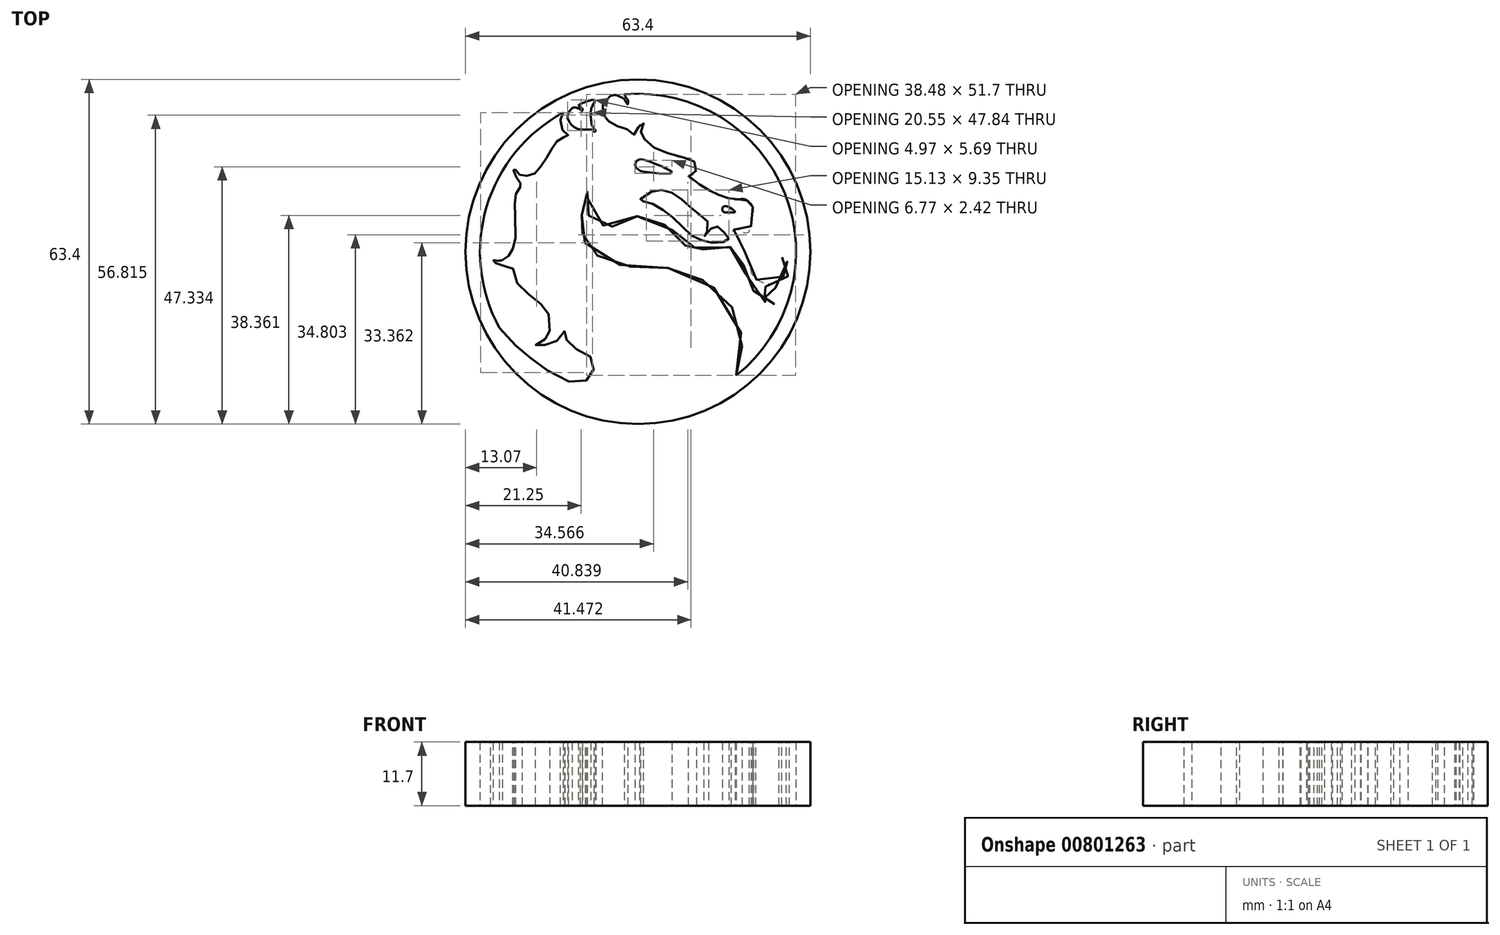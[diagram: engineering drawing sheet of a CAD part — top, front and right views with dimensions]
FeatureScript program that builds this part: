
annotation { "Feature Type Name" : "Feature", "Feature Type Description" : "" }
export const myFeature = defineFeature(function(context is Context, id is Id, definition is map)
    precondition{}
    {
        {
            var Q0;
            Q0=qCreatedBy(makeId("Top.planeOp"),FACE);
            var sketch = newSketch(context, id + "F0", { "sketchPlane" : qUnion([Q0])});
            skCircle(sketch, "E0", {"center": v(0, 0) * mm, "radius": 31.7 * mm});
            skArc(sketch, "E1", {"start": v(-7.96, 27.95) * mm, "mid": v(-9.46, 27.48) * mm, "end": v(-10.93, 26.93) * mm});
            skFitSpline(sketch, "E2", {"points": [v(-25.5, -13.95) * mm, v(-22.7, -17.05) * mm, v(-20.86, -18.67) * mm, v(-18.36, -20.6) * mm, v(-15.95, -22.27) * mm, v(-12.36, -23.98) * mm, v(-10.16, -23.98) * mm, v(-8.94, -23.23) * mm, v(-8.32, -22.18) * mm, v(-8.02, -20.95) * mm, v(-8.32, -19.72) * mm, v(-9.99, -18.54) * mm, v(-11.26, -17.93) * mm, v(-12.22, -17.23) * mm, v(-13.1, -16.26) * mm, v(-13.4, -15.12) * mm, v(-13.4, -14.46) * mm, v(-13.67, -14.9) * mm, v(-14.24, -15.78) * mm, v(-15.03, -16.48) * mm, v(-15.9, -16.96) * mm, v(-17.22, -17.18) * mm, v(-18.06, -17.31) * mm, v(-18.85, -17.31) * mm, v(-18.67, -17.05) * mm, v(-17.88, -16.61) * mm, v(-17.14, -16.13) * mm, v(-16.74, -15.7) * mm, v(-16.52, -15.16) * mm, v(-16.26, -14.6) * mm, v(-16.21, -12.23) * mm, v(-16.54, -11.21) * mm, v(-17.22, -10.16) * mm, v(-18.21, -9.34) * mm, v(-19.41, -8.4) * mm, v(-20.9, -7.06) * mm, v(-22.02, -5.97) * mm, v(-22.84, -4.63) * mm, v(-22.95, -3.05) * mm, v(-22.8, -2.6) * mm, v(-23.37, -2.72) * mm, v(-24.22, -2.82) * mm, v(-25.2, -2.63) * mm, v(-26.25, -2.07) * mm, v(-27.1, -1.5) * mm, v(-27.02, -1.3) * mm, v(-26.62, -1.56) * mm], "startDerivative": vector(73.14, -85.9) * mm, "endDerivative": vector(33.12, -30.6) * mm});
            skArc(sketch, "E3", {"start": v(-26.62, -1.56) * mm, "mid": v(-25.76, -1.65) * mm, "end": v(-24.9, -1.56) * mm});
            skFitSpline(sketch, "E4", {"points": [v(-24.9, -1.56) * mm, v(-24.22, -1.18) * mm, v(-23.58, -0.47) * mm, v(-23.09, 0.44) * mm, v(-22.64, 1.15) * mm, v(-22.61, 7.55) * mm, v(-22.64, 8.78) * mm, v(-22.5, 10.34) * mm, v(-22.04, 11.46) * mm, v(-21.33, 12.17) * mm, v(-21.23, 12.27) * mm, v(-21.7, 12.74) * mm, v(-22.17, 13.42) * mm, v(-22.64, 14.17) * mm, v(-22.87, 14.98) * mm, v(-22.87, 15.55) * mm, v(-22.59, 15.16) * mm, v(-22.12, 14.54) * mm, v(-21.67, 14.15) * mm, v(-20.92, 13.94) * mm, v(-19.85, 14.02) * mm, v(-18.9, 14.46) * mm, v(-18.1, 15.37) * mm, v(-17.27, 16.54) * mm, v(-16.2, 18.27) * mm, v(-15.6, 19.39) * mm, v(-14.82, 20.4) * mm, v(-13.93, 21.03) * mm, v(-12.94, 21.13) * mm, v(-12.76, 21.34) * mm, v(-13.23, 21.6) * mm, v(-13.9, 22.49) * mm, v(-14.24, 24.05) * mm, v(-14, 25.12) * mm, v(-13.7, 25.63) * mm, v(-13.68, 25.64) * mm, v(-13.7, 25.63) * mm], "startDerivative": vector(27.03, 13) * mm, "endDerivative": vector(-4.63, -2.23) * mm});
            skFitSpline(sketch, "E5", {"points": [v(-7.96, 27.95) * mm, v(-7.98, 27.45) * mm, v(-8.51, 26.58) * mm, v(-8.66, 25.66) * mm, v(-8.64, 24.6) * mm, v(-8.59, 23.87) * mm, v(-8.35, 23.06) * mm, v(-8.01, 22.6) * mm, v(-7.74, 22.29) * mm, v(-7.94, 22.07) * mm, v(-8.42, 22.43) * mm, v(-8.9, 22.47) * mm, v(-10.1, 22.45) * mm, v(-11.04, 22.56) * mm, v(-11.98, 23.08) * mm, v(-12.59, 23.82) * mm, v(-12.95, 24.76) * mm, v(-12.72, 25.66) * mm, v(-11.93, 26.5) * mm, v(-11, 26.4) * mm, v(-10.5, 26.12) * mm, v(-10.36, 25.83) * mm, v(-10.19, 26.21) * mm, v(-10.45, 26.55) * mm, v(-10.8, 26.8) * mm, v(-10.93, 26.93) * mm, v(-7.96, 27.95) * mm]});
            skFitSpline(sketch, "E6", {"points": [v(-2.48, 28.95) * mm, v(-2.35, 28.65) * mm, v(-2.13, 28.23) * mm, v(-1.99, 28.1) * mm, v(-1.84, 27.77) * mm, v(-1.9, 27.08) * mm, v(-2.17, 27.53) * mm, v(-2.65, 28.17) * mm, v(-3.07, 28.43) * mm, v(-3.52, 28.61) * mm, v(-3.9, 28.8) * mm, v(-5.2, 28.6) * mm, v(-6, 27.86) * mm, v(-6.43, 27.08) * mm, v(-6.5, 26.48) * mm, v(-6.48, 25.57) * mm, v(-6.28, 25.02) * mm, v(-5.99, 24.56) * mm, v(-5.4, 24.02) * mm, v(-4.7, 23.6) * mm, v(-3.96, 23.23) * mm, v(-3.33, 22.92) * mm, v(-2.48, 22.7) * mm, v(-1.7, 22.35) * mm, v(-1.1, 21.89) * mm, v(-0.75, 21.52) * mm, v(-0.46, 22.2) * mm, v(-0.16, 22.68) * mm, v(0.26, 23.12) * mm, v(0.69, 23.7) * mm, v(1, 23.71) * mm, v(1.02, 23.71) * mm, v(0.96, 23.23) * mm, v(0.72, 22.72) * mm, v(0.56, 21.98) * mm, v(0.72, 21.39) * mm, v(0.94, 21.02) * mm, v(1.38, 20.55) * mm, v(2.37, 19.56) * mm, v(3.61, 18.87) * mm, v(5.26, 18.2) * mm, v(7.33, 17.45) * mm, v(9.38, 17.26) * mm, v(10.03, 16.9) * mm, v(10.74, 15.96) * mm, v(10.78, 15.4) * mm, v(10.53, 14.66) * mm, v(9.97, 14.25) * mm, v(9.57, 14) * mm, v(9.29, 13.82) * mm, v(10.76, 12.74) * mm, v(12.49, 11.67) * mm, v(13.12, 11.27) * mm, v(13.74, 10.96) * mm, v(14.4, 10.7) * mm, v(15.2, 10.29) * mm, v(16.17, 9.97) * mm, v(16.86, 9.8) * mm, v(17.82, 9.66) * mm, v(18.56, 9.64) * mm, v(19.11, 9.7) * mm, v(19.73, 9.59) * mm, v(20.34, 9.22) * mm, v(20.81, 8.74) * mm, v(21.1, 8.24) * mm, v(21.09, 8.23) * mm], "startDerivative": vector(11.35, -25.78) * mm, "endDerivative": vector(-1.39, -4.3) * mm});
            skFitSpline(sketch, "E7", {"points": [v(21.1, 8.23) * mm, v(21.3, 7.6) * mm, v(20.78, 6.66) * mm, v(20.5, 6.47) * mm, v(20.73, 6.03) * mm, v(20.84, 5.17) * mm, v(20.42, 3.7) * mm, v(19.9, 3.18) * mm, v(19.43, 3.6) * mm, v(18.65, 3.98) * mm, v(17.69, 4.04) * mm, v(17.2, 3.96) * mm, v(17.87, 3.36) * mm, v(18.64, 2.35) * mm, v(19.33, 0.75) * mm, v(20, -0.85) * mm, v(20.52, -2.6) * mm, v(21.1, -4.44) * mm, v(22.36, -5.44) * mm, v(23.93, -5.93) * mm, v(25.25, -5.72) * mm, v(26.43, -4.89) * mm, v(27.16, -3.5) * mm, v(27.1, -2.17) * mm, v(26.47, -1.03) * mm, v(27.2, -1.48) * mm, v(27.8, -2.9) * mm, v(27.55, -4.57) * mm, v(26.36, -6.07) * mm, v(24.24, -6.66) * mm, v(21.77, -6.04) * mm, v(22.3, -7.53) * mm, v(24.03, -8.79) * mm, v(25.7, -9.27) * mm, v(25.95, -9.48) * mm, v(24.62, -9.59) * mm, v(22.85, -8.96) * mm, v(21.5, -7.57) * mm, v(20.27, -5.51) * mm, v(19.61, -3.29) * mm, v(18.88, -0.78) * mm, v(17.77, 1.17) * mm, v(16.69, 0.65) * mm, v(14.22, -0.26) * mm, v(11.82, 0.5) * mm, v(10.08, 0.68) * mm, v(9.17, 0.37) * mm, v(8.69, 1.27) * mm, v(6.84, 3.57) * mm, v(4.86, 4.96) * mm, v(2.28, 6.42) * mm, v(0, 6.56) * mm, v(-2.42, 5.7) * mm, v(-4.16, 4.75) * mm, v(-6.28, 4.79) * mm, v(-8.33, 5.8) * mm, v(-9.44, 7.64) * mm, v(-9.44, 10.32) * mm, v(-9.24, 11.02) * mm, v(-9.97, 10.11) * mm, v(-10.56, 8.23) * mm, v(-10.04, 6.21) * mm, v(-9.37, 5.38) * mm, v(-9.86, 4.82) * mm, v(-10.07, 2.63) * mm, v(-9.1, 0.71) * mm, v(-7.29, -0.82) * mm, v(-3.42, -2.35) * mm, v(-0.43, -2.8) * mm, v(4.1, -2.8) * mm, v(8.3, -3.67) * mm, v(12.06, -5.3) * mm, v(15.89, -8.5) * mm, v(18.4, -12.47) * mm, v(19.16, -17.42) * mm, v(18.9, -20.57) * mm, v(18.08, -22.75) * mm, v(18.05, -22.78) * mm], "startDerivative": vector(44.78, -70.7) * mm, "endDerivative": vector(-14.23, -4.64) * mm});
            skPoint(sketch, "E8", {"position": v(-12.1, 26.41) * mm});
            skPoint(sketch, "E9", {"position": v(-11.83, 26.52) * mm});
            skPoint(sketch, "E10", {"position": v(-13.74, 25.58) * mm});
            skFitSpline(sketch, "E11.trimOffspring", {"points": [v(-2.48, 28.95) * mm, v(-2.35, 28.65) * mm, v(-2.13, 28.23) * mm, v(-1.99, 28.1) * mm, v(-1.84, 27.77) * mm, v(-1.9, 27.08) * mm, v(-2.17, 27.53) * mm, v(-2.65, 28.17) * mm, v(-3.07, 28.43) * mm, v(-3.52, 28.61) * mm, v(-3.9, 28.8) * mm, v(-5.2, 28.6) * mm, v(-6, 27.86) * mm, v(-6.43, 27.08) * mm, v(-6.5, 26.48) * mm, v(-6.48, 25.57) * mm, v(-6.28, 25.02) * mm, v(-5.99, 24.56) * mm, v(-5.4, 24.02) * mm, v(-4.7, 23.6) * mm, v(-3.96, 23.23) * mm, v(-3.33, 22.92) * mm, v(-2.48, 22.7) * mm, v(-1.7, 22.35) * mm, v(-1.1, 21.89) * mm, v(-0.75, 21.52) * mm, v(-0.46, 22.2) * mm, v(-0.16, 22.68) * mm, v(0.26, 23.12) * mm, v(0.69, 23.7) * mm, v(1, 23.71) * mm, v(1.02, 23.71) * mm, v(0.96, 23.23) * mm, v(0.72, 22.72) * mm, v(0.56, 21.98) * mm, v(0.72, 21.39) * mm, v(0.94, 21.02) * mm, v(1.38, 20.55) * mm, v(2.37, 19.56) * mm, v(3.61, 18.87) * mm, v(5.26, 18.2) * mm, v(7.33, 17.45) * mm, v(9.38, 17.26) * mm, v(10.03, 16.9) * mm, v(10.74, 15.96) * mm, v(10.78, 15.4) * mm, v(10.53, 14.66) * mm, v(9.97, 14.25) * mm, v(9.57, 14) * mm, v(9.29, 13.82) * mm, v(10.76, 12.74) * mm, v(12.49, 11.67) * mm, v(13.12, 11.27) * mm, v(13.74, 10.96) * mm, v(14.4, 10.7) * mm, v(15.2, 10.29) * mm, v(16.17, 9.97) * mm, v(16.86, 9.8) * mm, v(17.82, 9.66) * mm, v(18.56, 9.64) * mm, v(19.11, 9.7) * mm, v(19.73, 9.59) * mm, v(20.34, 9.22) * mm, v(20.81, 8.74) * mm, v(21.1, 8.24) * mm, v(21.09, 8.23) * mm], "startDerivative": vector(11.35, -25.78) * mm, "endDerivative": vector(-1.39, -4.3) * mm});
            skArc(sketch, "E12.trimOffspring", {"start": v(-3.9, 28.8) * mm, "mid": v(-4.55, 28.7) * mm, "end": v(-5.2, 28.6) * mm});
            skArc(sketch, "E13.trimOffspring", {"start": v(18.08, -22.75) * mm, "mid": v(27, 10.74) * mm, "end": v(-2.48, 28.95) * mm});
            skLineSegment(sketch, "E14", {"start": v(-12.1, 26.41) * mm, "end": v(-11.83, 26.52) * mm});
            skArc(sketch, "E15", {"start": v(-13.74, 25.58) * mm, "mid": v(-27.82, 8.25) * mm, "end": v(-25.5, -13.95) * mm});
            skFitSpline(sketch, "E16", {"points": [v(6.25, 14.54) * mm, v(1.57, 16.78) * mm, v(0, 16.86) * mm, v(-0.56, 15.95) * mm, v(0, 15.19) * mm, v(0.58, 14.82) * mm, v(1.46, 14.68) * mm, v(6.25, 14.54) * mm]});
            skFitSpline(sketch, "E17", {"points": [v(17.84, 7.32) * mm, v(16.29, 8.38) * mm, v(15.53, 8) * mm, v(15.76, 7.32) * mm, v(17.3, 7.25) * mm, v(17.84, 7.32) * mm]});
            skFitSpline(sketch, "E18", {"points": [v(16.7, 2.4) * mm, v(16.25, 1.91) * mm, v(14.28, 1.65) * mm, v(12, 1.99) * mm, v(9.66, 3.16) * mm, v(7.2, 5.58) * mm, v(4.78, 7.55) * mm, v(2.35, 8.95) * mm, v(0.73, 9.25) * mm, v(0.27, 9.4) * mm, v(2.43, 11) * mm, v(4.44, 11.34) * mm, v(6.7, 10.62) * mm, v(9.02, 8.76) * mm, v(11.36, 6.72) * mm, v(12.69, 5.73) * mm, v(12.8, 3.92) * mm, v(12.12, 3) * mm, v(12.5, 2.93) * mm, v(13.9, 4.83) * mm, v(14.92, 4.4) * mm, v(16.06, 3.39) * mm, v(16.7, 2.4) * mm]});
            skSolve(sketch);
        }
        {
            var Q0;
            Q0=qSketchRegion(id+"F0",true);
            extrude(context, id + "F1", {"entities" : qUnion([Q0]), "depth" : 11.7 * mm, "offsetDistance" : 25 * mm});
        }
    });
